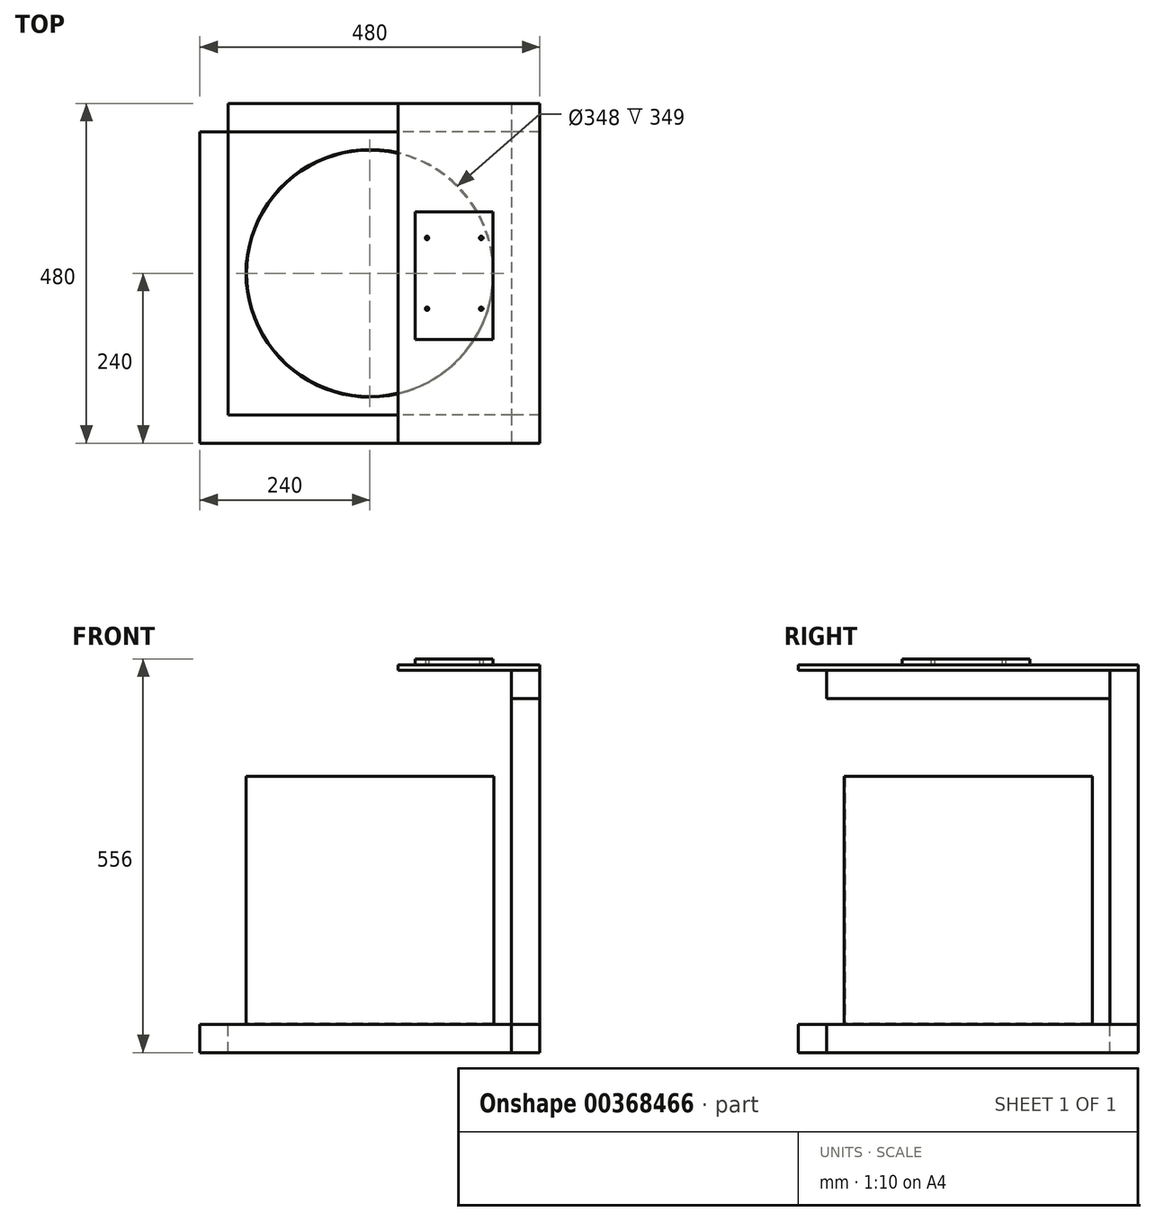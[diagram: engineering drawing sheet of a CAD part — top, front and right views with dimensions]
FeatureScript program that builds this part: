
annotation { "Feature Type Name" : "Feature", "Feature Type Description" : "" }
export const myFeature = defineFeature(function(context is Context, id is Id, definition is map)
    precondition{}
    {
        {
            var Q0;
            Q0=qCreatedBy(makeId("Top.planeOp"),FACE);
            var sketch = newSketch(context, id + "F0", { "sketchPlane" : qUnion([Q0])});
            skLineSegment(sketch, "E0.bottom", {"start": v(200, 200) * mm, "end": v(-200, 200) * mm});
            skLineSegment(sketch, "E0.top", {"start": v(200, -200) * mm, "end": v(-200, -200) * mm});
            skLineSegment(sketch, "E0.left", {"start": v(200, 200) * mm, "end": v(200, -200) * mm});
            skLineSegment(sketch, "E0.right", {"start": v(-200, 200) * mm, "end": v(-200, -200) * mm});
            skPoint(sketch, "E0.middle", {"position": v(0, 0) * mm});
            skLineSegment(sketch, "E1.0", {"start": v(240, 240) * mm, "end": v(240, -240) * mm});
            skLineSegment(sketch, "E1.1", {"start": v(240, 240) * mm, "end": v(-240, 240) * mm});
            skLineSegment(sketch, "E1.2", {"start": v(-240, 240) * mm, "end": v(-240, -240) * mm});
            skLineSegment(sketch, "E1.3", {"start": v(240, -240) * mm, "end": v(-240, -240) * mm});
            skLineSegment(sketch, "E2.bottom", {"start": v(-240, 240) * mm, "end": v(-200, 240) * mm});
            skLineSegment(sketch, "E2.top", {"start": v(-240, 200) * mm, "end": v(-200, 200) * mm});
            skLineSegment(sketch, "E2.left", {"start": v(-240, 240) * mm, "end": v(-240, 200) * mm});
            skLineSegment(sketch, "E2.right", {"start": v(-200, 240) * mm, "end": v(-200, 200) * mm});
            skLineSegment(sketch, "E3.0.1.0", {"start": v(-240, -240) * mm, "end": v(-200, -240) * mm});
            skLineSegment(sketch, "E3.0.1.1", {"start": v(-240, -200) * mm, "end": v(-200, -200) * mm});
            skLineSegment(sketch, "E3.0.1.2", {"start": v(-240, -200) * mm, "end": v(-240, -240) * mm});
            skLineSegment(sketch, "E3.1.0.0", {"start": v(200, 200) * mm, "end": v(240, 200) * mm});
            skLineSegment(sketch, "E3.1.0.1", {"start": v(200, 240) * mm, "end": v(240, 240) * mm});
            skLineSegment(sketch, "E3.1.0.2", {"start": v(200, 240) * mm, "end": v(200, 200) * mm});
            skLineSegment(sketch, "E3.1.1.0", {"start": v(200, -240) * mm, "end": v(240, -240) * mm});
            skLineSegment(sketch, "E3.1.1.1", {"start": v(200, -200) * mm, "end": v(240, -200) * mm});
            skLineSegment(sketch, "E3.1.1.2", {"start": v(200, -200) * mm, "end": v(200, -240) * mm});
            skLineSegment(sketch, "E3.direction1", {"start": v(-240, 200) * mm, "end": v(200, 200) * mm, "construction": true});
            skLineSegment(sketch, "E3.direction2", {"start": v(-240, 200) * mm, "end": v(-240, -240) * mm, "construction": true});
            skSolve(sketch);
        }
        {
            var Q0;
            Q0=makeQuery(id+"F0.imprint","IMPRINT",FACE,{"disambiguationData":[TD([[makeQuery(id+"F0.imprint","IMPRINT",EDGE,{"derivedFrom":sQuery(id+"F0.wireOp",EDGE,"E0.bottom")}),-1.0]])]});
            var Q1;
            {var subQ2=sQuery(id+"F0.wireOp",EDGE,"E3.1.0.0");Q1=makeQuery(id+"F0.imprint","IMPRINT",FACE,{"disambiguationData":[TD([[makeQuery(id+"F0.imprint","IMPRINT",EDGE,{"derivedFrom":subQ2}),1.0]])]});}
            var Q2;
            Q2=makeQuery(id+"F0.imprint","IMPRINT",FACE,{"disambiguationData":[TD([[makeQuery(id+"F0.imprint","IMPRINT",EDGE,{"derivedFrom":sQuery(id+"F0.wireOp",EDGE,"E0.left")}),1.0]])]});
            var Q3;
            {var subQ0=sQuery(id+"F0.wireOp",EDGE,"E3.1.1.0");Q3=makeQuery(id+"F0.imprint","IMPRINT",FACE,{"disambiguationData":[TD([[makeQuery(id+"F0.imprint","IMPRINT",EDGE,{"derivedFrom":subQ0}),1.0]])]});}
            var Q4;
            Q4=makeQuery(id+"F0.imprint","IMPRINT",FACE,{"disambiguationData":[TD([[makeQuery(id+"F0.imprint","IMPRINT",EDGE,{"derivedFrom":sQuery(id+"F0.wireOp",EDGE,"E0.right")}),-1.0]])]});
            var Q5;
            Q5=makeQuery(id+"F0.imprint","IMPRINT",FACE,{"disambiguationData":[TD([[makeQuery(id+"F0.imprint","IMPRINT",EDGE,{"derivedFrom":sQuery(id+"F0.wireOp",EDGE,"E2.bottom")}),-1.0]])]});
            var Q6;
            Q6=makeQuery(id+"F0.imprint","IMPRINT",FACE,{"disambiguationData":[TD([[makeQuery(id+"F0.imprint","IMPRINT",EDGE,{"derivedFrom":sQuery(id+"F0.wireOp",EDGE,"E0.top")}),1.0]])]});
            extrude(context, id + "F1", {"entities" : qUnion([Q0, Q1, Q2, Q3, Q4, Q5, Q6]), "oppositeDirection" : true, "depth" : 40 * mm});
        }
        {
            var Q0;
            {var subQ2=sQuery(id+"F0.wireOp",EDGE,"E3.1.0.0");Q0=makeQuery(id+"F0.imprint","IMPRINT",FACE,{"disambiguationData":[TD([[makeQuery(id+"F0.imprint","IMPRINT",EDGE,{"derivedFrom":subQ2}),1.0]])]});}
            var Q1;
            {var subQ0=sQuery(id+"F0.wireOp",EDGE,"E3.1.1.0");Q1=makeQuery(id+"F0.imprint","IMPRINT",FACE,{"disambiguationData":[TD([[makeQuery(id+"F0.imprint","IMPRINT",EDGE,{"derivedFrom":subQ0}),1.0]])]});}
            extrude(context, id + "F2", {"entities" : qUnion([Q0, Q1]), "depth" : 500 * mm});
        }
        {
            var Q0;
            Q0=qCreatedBy(makeId("Top.planeOp"),FACE);
            var Q1;
            Q1=makeQuery(id+"F2.opExtrude","CAP_VERTEX",VERTEX,{"disambiguationData":[OSD([sQuery(id+"F0.wireOp",EDGE,"E1.0"),sQuery(id+"F0.wireOp",EDGE,"E3.1.0.0")])],"isStart":false});
            cPlane(context, id + "F3", {"entities" : qUnion([Q0, Q1]), "cplaneType" : CPlaneType.PLANE_POINT, "offset" : 540 * mm, "width" : 150 * mm, "height" : 150 * mm});
        }
        {
            var Q0;
            Q0=qCreatedBy(id+"F3.planeOp",FACE);
            var sketch = newSketch(context, id + "F4", { "sketchPlane" : qUnion([Q0])});
            skPoint(sketch, "E4.0", {"position": v(240, 200) * mm});
            skPoint(sketch, "E5.0", {"position": v(200, -200) * mm});
            skLineSegment(sketch, "E6.bottom", {"start": v(240, 200) * mm, "end": v(200, 200) * mm});
            skLineSegment(sketch, "E6.top", {"start": v(240, -200) * mm, "end": v(200, -200) * mm});
            skLineSegment(sketch, "E6.left", {"start": v(240, 200) * mm, "end": v(240, -200) * mm});
            skLineSegment(sketch, "E6.right", {"start": v(200, 200) * mm, "end": v(200, -200) * mm});
            skLineSegment(sketch, "E7.0", {"start": v(240, 240) * mm, "end": v(240, -240) * mm});
            skLineSegment(sketch, "E8.0", {"start": v(240, 240) * mm, "end": v(40, 240) * mm});
            skLineSegment(sketch, "E9.0", {"start": v(240, -240) * mm, "end": v(40, -240) * mm});
            skLineSegment(sketch, "E10", {"start": v(-240, 0) * mm, "end": v(240, 0) * mm, "construction": true});
            skLineSegment(sketch, "E11.0", {"start": v(40, 240) * mm, "end": v(40, -240) * mm});
            skSolve(sketch);
        }
        {
            var Q0;
            Q0=makeQuery(id+"F4.imprint","IMPRINT",FACE,{"disambiguationData":[TD([[makeQuery(id+"F4.imprint","IMPRINT",EDGE,{"derivedFrom":sQuery(id+"F4.wireOp",EDGE,"E6.bottom")}),1.0]])]});
            extrude(context, id + "F5", {"entities" : qUnion([Q0]), "oppositeDirection" : true, "depth" : 40 * mm});
        }
        {
            var Q0;
            Q0=qCreatedBy(makeId("Top.planeOp"),FACE);
            var sketch = newSketch(context, id + "F6", { "sketchPlane" : qUnion([Q0])});
            skCircle(sketch, "E12", {"center": v(0, 0) * mm, "radius": 175 * mm});
            skSolve(sketch);
        }
        {
            var Q0;
            Q0=makeQuery(id+"F6.imprint","IMPRINT",FACE,{"disambiguationData":[TD([[makeQuery(id+"F6.imprint","IMPRINT",EDGE,{"derivedFrom":sQuery(id+"F6.wireOp",EDGE,"E12")}),1.0]])]});
            extrude(context, id + "F7", {"entities" : qUnion([Q0]), "depth" : 350 * mm});
        }
        {
            var Q0;
            Q0=makeQuery(id+"F7.opExtrude","CAP_FACE",FACE,{"disambiguationData":[OSD([sQuery(id+"F6.wireOp",EDGE,"E12")])],"isStart":false});
            shell(context, id + "F8", {"entities" : qUnion([Q0]), "thickness" : (1) * mm});
        }
        {
            var Q0;
            {var subQ1=sQuery(id+"F4.wireOp",EDGE,"E6.bottom");Q0=makeQuery(id+"F4.imprint","IMPRINT",FACE,{"disambiguationData":[TD([[makeQuery(id+"F4.imprint","IMPRINT",EDGE,{"derivedFrom":subQ1}),-1.0]])]});}
            var Q1;
            {var subQ0=sQuery(id+"F4.wireOp",EDGE,"E6.bottom");Q1=makeQuery(id+"F4.imprint","IMPRINT",FACE,{"disambiguationData":[TD([[makeQuery(id+"F4.imprint","IMPRINT",EDGE,{"derivedFrom":subQ0}),1.0]])]});}
            extrude(context, id + "F9", {"entities" : qUnion([Q0, Q1]), "depth" : 8 * mm});
        }
        {
            var Q0;
            Q0=makeQuery(id+"F9.opExtrude","CAP_FACE",FACE,{"disambiguationData":[OSD([sQuery(id+"F4.wireOp",EDGE,"E7.0"),sQuery(id+"F4.wireOp",EDGE,"E8.0"),sQuery(id+"F4.wireOp",EDGE,"E9.0"),sQuery(id+"F4.wireOp",EDGE,"E11.0")])],"isStart":false});
            var sketch = newSketch(context, id + "F10", { "sketchPlane" : qUnion([Q0])});
            skPoint(sketch, "E13.0", {"position": v(157.2, 0) * mm});
            skPoint(sketch, "E14.0", {"position": v(80.7, 0) * mm});
            skLineSegment(sketch, "E15.0", {"start": v(-240, 0) * mm, "end": v(240, 0) * mm, "construction": true});
            skCircle(sketch, "E16", {"center": v(157.2, -50) * mm, "radius": 2.5 * mm});
            skCircle(sketch, "E17", {"center": v(157.2, 50) * mm, "radius": 2.5 * mm});
            skCircle(sketch, "E18", {"center": v(80.7, -50) * mm, "radius": 2.5 * mm});
            skCircle(sketch, "E19", {"center": v(80.7, 50) * mm, "radius": 2.5 * mm});
            skLineSegment(sketch, "E20.bottom", {"start": v(63.95, -93.22) * mm, "end": v(173.95, -93.22) * mm});
            skLineSegment(sketch, "E20.top", {"start": v(63.95, 86.78) * mm, "end": v(173.95, 86.78) * mm});
            skLineSegment(sketch, "E20.left", {"start": v(63.95, -93.22) * mm, "end": v(63.95, 86.78) * mm});
            skLineSegment(sketch, "E20.right", {"start": v(173.95, -93.22) * mm, "end": v(173.95, 86.78) * mm});
            skSolve(sketch);
        }
        {
            var Q0;
            Q0=makeQuery(id+"F10.imprint","IMPRINT",FACE,{"disambiguationData":[TD([[makeQuery(id+"F10.imprint","IMPRINT",EDGE,{"derivedFrom":sQuery(id+"F10.wireOp",EDGE,"E16")}),-1.0]])]});
            extrude(context, id + "F11", {"entities" : qUnion([Q0]), "depth" : 8 * mm});
        }
    });
